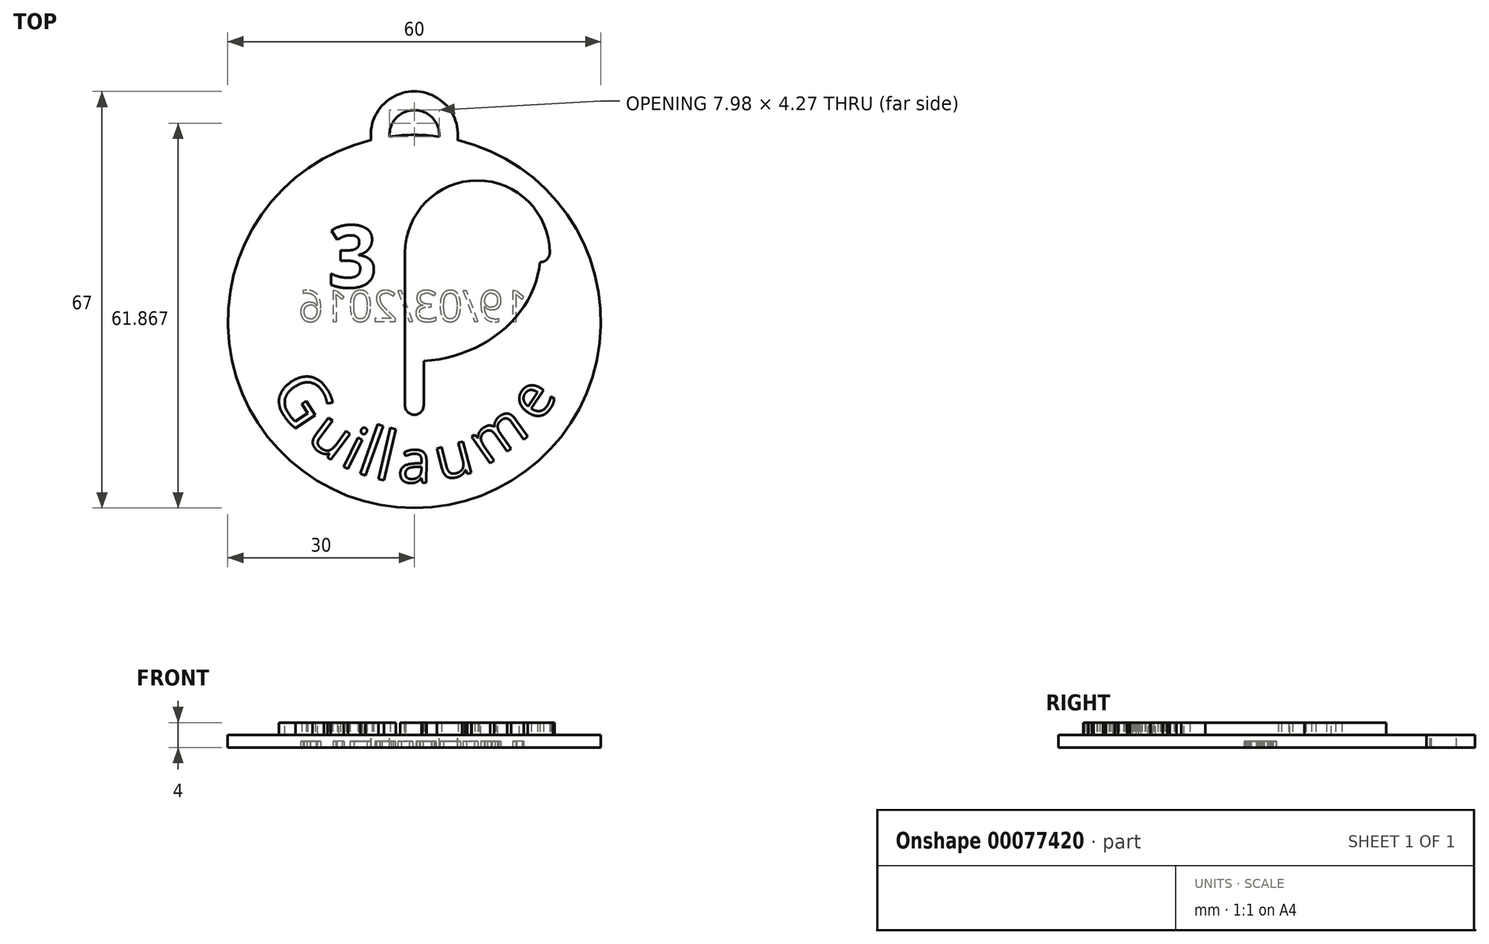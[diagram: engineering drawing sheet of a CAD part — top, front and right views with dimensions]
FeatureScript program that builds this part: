
annotation { "Feature Type Name" : "Feature", "Feature Type Description" : "" }
export const myFeature = defineFeature(function(context is Context, id is Id, definition is map)
    precondition{}
    {
        {
            var Q0;
            Q0=qCreatedBy(makeId("Top.planeOp"),FACE);
            var sketch = newSketch(context, id + "F0", { "sketchPlane" : qUnion([Q0])});
            skCircle(sketch, "E0", {"center": v(0, 0) * mm, "radius": 30 * mm});
            skSolve(sketch);
        }
        {
            var Q0;
            Q0=qSketchRegion(id+"F0",true);
            extrude(context, id + "F1", {"entities" : qUnion([Q0]), "oppositeDirection" : true, "depth" : 2 * mm});
        }
        {
            var Q0;
            Q0=qCreatedBy(makeId("Top.planeOp"),FACE);
            var sketch = newSketch(context, id + "F2", { "sketchPlane" : qUnion([Q0])});
            skEllipticalArc(sketch, "E1", {});
            skLineSegment(sketch, "E2", {"start": v(0, 0) * mm, "end": v(0, 30) * mm, "construction": true});
            skLineSegment(sketch, "E3", {"start": v(0, 11.04) * mm, "end": v(0, -13.5) * mm});
            skArc(sketch, "E4", {"start": v(20.27, 11.04) * mm, "mid": v(10.13, 21.17) * mm, "end": v(0, 11.04) * mm});
            skLineSegment(sketch, "E5", {"start": v(0, 11.04) * mm, "end": v(-16.84, 20.76) * mm, "construction": true});
            skLineSegment(sketch, "E6", {"start": v(0, 11.04) * mm, "end": v(-20.27, 11.04) * mm, "construction": true});
            skArc(sketch, "E7.0.startCap", {"start": v(-1.5, 11.04) * mm, "mid": v(0, 12.54) * mm, "end": v(1.5, 11.04) * mm});
            skArc(sketch, "E7.0.endCap", {"start": v(1.5, -13.5) * mm, "mid": v(0, -15) * mm, "end": v(-1.5, -13.5) * mm});
            skLineSegment(sketch, "E7.0.left", {"start": v(1.5, 11.04) * mm, "end": v(1.5, -13.5) * mm});
            skLineSegment(sketch, "E7.0.right", {"start": v(-1.5, 11.04) * mm, "end": v(-1.5, -13.5) * mm});
            skArc(sketch, "E8.0.startCap", {"start": v(21.77, 11.04) * mm, "mid": v(20.27, 9.54) * mm, "end": v(18.77, 11.04) * mm});
            skArc(sketch, "E8.0.endCap", {"start": v(1.5, 11.04) * mm, "mid": v(0, 9.54) * mm, "end": v(-1.5, 11.04) * mm});
            skArc(sketch, "E8.0.left", {"start": v(18.77, 11.04) * mm, "mid": v(10.13, 19.67) * mm, "end": v(1.5, 11.04) * mm});
            skArc(sketch, "E8.0.right", {"start": v(21.77, 11.04) * mm, "mid": v(10.13, 22.67) * mm, "end": v(-1.5, 11.04) * mm});
            skArc(sketch, "E8.1.startCap", {"start": v(-18.02, 21.68) * mm, "mid": v(-15.91, 21.95) * mm, "end": v(-15.65, 19.84) * mm});
            skArc(sketch, "E8.1.endCap", {"start": v(18.77, 11.04) * mm, "mid": v(20.27, 12.54) * mm, "end": v(21.77, 11.04) * mm});
            skFitSpline(sketch, "E8.1.left", {"points": [v(18.7, 9.5) * mm, v(18.8, 11.04) * mm, v(18.7, 12.6) * mm, v(18.36, 14.63) * mm, v(17.66, 16.6) * mm, v(16.63, 18.49) * mm, v(15.37, 20.3) * mm, v(13.44, 22.32) * mm, v(11.07, 24) * mm, v(8.94, 25.1) * mm, v(6.7, 26.01) * mm, v(4.32, 26.63) * mm, v(1.87, 26.95) * mm, v(0, 27.03) * mm, v(-1.87, 26.95) * mm, v(-4.32, 26.63) * mm, v(-6.7, 26.01) * mm, v(-8.94, 25.1) * mm, v(-11.07, 24) * mm, v(-13.44, 22.32) * mm, v(-15.37, 20.3) * mm, v(-16.63, 18.49) * mm, v(-17.66, 16.6) * mm, v(-18.36, 14.63) * mm, v(-18.7, 12.6) * mm, v(-18.8, 11.04) * mm, v(-18.7, 9.5) * mm, v(-18.36, 7.46) * mm, v(-17.66, 5.48) * mm, v(-16.63, 3.6) * mm, v(-15.37, 1.8) * mm, v(-13.44, -0.24) * mm, v(-11.07, -1.92) * mm, v(-8.94, -3.02) * mm, v(-6.7, -3.93) * mm, v(-4.32, -4.55) * mm, v(-1.87, -4.86) * mm, v(0, -4.94) * mm, v(1.87, -4.86) * mm, v(4.32, -4.55) * mm, v(6.7, -3.93) * mm, v(8.94, -3.02) * mm, v(11.07, -1.92) * mm, v(13.44, -0.24) * mm, v(15.37, 1.8) * mm, v(16.63, 3.6) * mm, v(17.66, 5.48) * mm, v(18.36, 7.46) * mm, v(18.7, 9.5) * mm, v(18.8, 11.04) * mm, v(18.7, 12.6) * mm]});
            skFitSpline(sketch, "E8.1.right", {"points": [v(21.7, 9.15) * mm, v(21.8, 11.04) * mm, v(21.7, 12.93) * mm, v(21.27, 15.42) * mm, v(20.42, 17.81) * mm, v(19.18, 20.07) * mm, v(17.69, 22.22) * mm, v(15.4, 24.61) * mm, v(12.65, 26.56) * mm, v(10.2, 27.83) * mm, v(7.62, 28.88) * mm, v(4.92, 29.58) * mm, v(2.12, 29.94) * mm, v(0, 30.03) * mm, v(-2.12, 29.94) * mm, v(-4.92, 29.58) * mm, v(-7.62, 28.88) * mm, v(-10.2, 27.83) * mm, v(-12.65, 26.56) * mm, v(-15.4, 24.61) * mm, v(-17.69, 22.22) * mm, v(-19.18, 20.07) * mm, v(-20.42, 17.81) * mm, v(-21.27, 15.42) * mm, v(-21.7, 12.93) * mm, v(-21.8, 11.04) * mm, v(-21.7, 9.15) * mm, v(-21.27, 6.67) * mm, v(-20.42, 4.27) * mm, v(-19.18, 2) * mm, v(-17.69, -0.14) * mm, v(-15.4, -2.53) * mm, v(-12.65, -4.48) * mm, v(-10.2, -5.75) * mm, v(-7.62, -6.8) * mm, v(-4.92, -7.5) * mm, v(-2.12, -7.86) * mm, v(0, -7.95) * mm, v(2.12, -7.86) * mm, v(4.92, -7.5) * mm, v(7.62, -6.8) * mm, v(10.2, -5.75) * mm, v(12.65, -4.48) * mm, v(15.4, -2.53) * mm, v(17.69, -0.14) * mm, v(19.18, 2) * mm, v(20.42, 4.27) * mm, v(21.27, 6.67) * mm, v(21.7, 9.15) * mm, v(21.8, 11.04) * mm, v(21.7, 12.93) * mm]});
            const initialGuessF2  = {"E1": [0, 0.011041626236194823, 1, 0, 0.020266667008310185, 0.017458373763805178, 2.5511335140588507, 0]};
            skSetInitialGuess(sketch, initialGuessF2);
            skSolve(sketch);
        }
        {
            var Q0;
            {var subQ0=sQuery(id+"F2.wireOp",EDGE,"E8.1.startCap");Q0=makeQuery(id+"F2.imprint","IMPRINT",FACE,{"disambiguationData":[TD([[makeQuery(id+"F2.imprint","IMPRINT",EDGE,{"derivedFrom":subQ0}),-1.0]])]});}
            var Q1;
            {var subQ0=sQuery(id+"F2.wireOp",EDGE,"E7.0.right");var subQ1=sQuery(id+"F2.wireOp",EDGE,"E1");var subQ2=makeQuery(id+"F2.imprint","INTERSECT",VERTEX,{"derivedFrom":[subQ1,subQ0]});Q1=makeQuery(id+"F2.imprint","IMPRINT",FACE,{"disambiguationData":[TD([[makeQuery(id+"F2.imprint","IMPRINT",EDGE,{"disambiguationData":[TD([[subQ2,-1.0]])],"derivedFrom":subQ1}),1.0]])]});}
            var Q2;
            {var subQ0=sQuery(id+"F2.wireOp",EDGE,"E3");var subQ1=sQuery(id+"F2.wireOp",EDGE,"E1");var subQ2=makeQuery(id+"F2.imprint","INTERSECT",VERTEX,{"derivedFrom":[subQ1,subQ0]});Q2=makeQuery(id+"F2.imprint","IMPRINT",FACE,{"disambiguationData":[TD([[makeQuery(id+"F2.imprint","IMPRINT",EDGE,{"disambiguationData":[TD([[subQ2,-1.0]])],"derivedFrom":subQ1}),1.0]])]});}
            var Q3;
            {var subQ0=sQuery(id+"F2.wireOp",EDGE,"E7.0.right");var subQ1=sQuery(id+"F2.wireOp",EDGE,"E1");var subQ2=makeQuery(id+"F2.imprint","INTERSECT",VERTEX,{"derivedFrom":[subQ1,subQ0]});Q3=makeQuery(id+"F2.imprint","IMPRINT",FACE,{"disambiguationData":[TD([[makeQuery(id+"F2.imprint","IMPRINT",EDGE,{"disambiguationData":[TD([[subQ2,-1.0]])],"derivedFrom":subQ1}),-1.0]])]});}
            var Q4;
            {var subQ0=sQuery(id+"F2.wireOp",EDGE,"E3");var subQ1=sQuery(id+"F2.wireOp",EDGE,"E1");var subQ2=makeQuery(id+"F2.imprint","INTERSECT",VERTEX,{"derivedFrom":[subQ1,subQ0]});Q4=makeQuery(id+"F2.imprint","IMPRINT",FACE,{"disambiguationData":[TD([[makeQuery(id+"F2.imprint","IMPRINT",EDGE,{"disambiguationData":[TD([[subQ2,-1.0]])],"derivedFrom":subQ1}),-1.0]])]});}
            var Q5;
            {var subQ0=sQuery(id+"F2.wireOp",EDGE,"E7.0.left");var subQ1=sQuery(id+"F2.wireOp",EDGE,"E1");var subQ2=makeQuery(id+"F2.imprint","INTERSECT",VERTEX,{"derivedFrom":[subQ1,subQ0]});Q5=makeQuery(id+"F2.imprint","IMPRINT",FACE,{"disambiguationData":[TD([[makeQuery(id+"F2.imprint","IMPRINT",EDGE,{"disambiguationData":[TD([[subQ2,-1.0]])],"derivedFrom":subQ1}),-1.0]])]});}
            var Q6;
            {var subQ0=sQuery(id+"F2.wireOp",EDGE,"E7.0.left");var subQ1=sQuery(id+"F2.wireOp",EDGE,"E1");var subQ2=makeQuery(id+"F2.imprint","INTERSECT",VERTEX,{"derivedFrom":[subQ1,subQ0]});Q6=makeQuery(id+"F2.imprint","IMPRINT",FACE,{"disambiguationData":[TD([[makeQuery(id+"F2.imprint","IMPRINT",EDGE,{"disambiguationData":[TD([[subQ2,-1.0]])],"derivedFrom":subQ1}),1.0]])]});}
            var Q7;
            {var subQ0=sQuery(id+"F2.wireOp",EDGE,"E4");var subQ1=sQuery(id+"F2.wireOp",EDGE,"E1");var subQ2=makeQuery(id+"F2.imprint","INTERSECT",VERTEX,{"derivedFrom":[subQ1,subQ0]});Q7=makeQuery(id+"F2.imprint","IMPRINT",FACE,{"disambiguationData":[TD([[makeQuery(id+"F2.imprint","IMPRINT",EDGE,{"disambiguationData":[TD([[subQ2,1.0]])],"derivedFrom":subQ1}),-1.0]])]});}
            var Q8;
            {var subQ0=sQuery(id+"F2.wireOp",EDGE,"E4");var subQ1=sQuery(id+"F2.wireOp",EDGE,"E1");var subQ2=makeQuery(id+"F2.imprint","INTERSECT",VERTEX,{"derivedFrom":[subQ1,subQ0]});Q8=makeQuery(id+"F2.imprint","IMPRINT",FACE,{"disambiguationData":[TD([[makeQuery(id+"F2.imprint","IMPRINT",EDGE,{"disambiguationData":[TD([[subQ2,1.0]])],"derivedFrom":subQ1}),1.0]])]});}
            var Q9;
            {var subQ5=sQuery(id+"F2.wireOp",EDGE,"E8.0.left");Q9=makeQuery(id+"F2.imprint","IMPRINT",FACE,{"disambiguationData":[TD([[makeQuery(id+"F2.imprint","IMPRINT",EDGE,{"derivedFrom":subQ5}),-1.0]])]});}
            var Q10;
            {var subQ5=sQuery(id+"F2.wireOp",EDGE,"E8.0.right");Q10=makeQuery(id+"F2.imprint","IMPRINT",FACE,{"disambiguationData":[TD([[makeQuery(id+"F2.imprint","IMPRINT",EDGE,{"derivedFrom":subQ5}),1.0]])]});}
            var Q11;
            {var subQ0=sQuery(id+"F2.wireOp",EDGE,"E4");var subQ1=sQuery(id+"F2.wireOp",EDGE,"E3");var subQ2=makeQuery(id+"F2.imprint","INTERSECT",VERTEX,{"derivedFrom":[subQ1,subQ0]});Q11=makeQuery(id+"F2.imprint","IMPRINT",FACE,{"disambiguationData":[TD([[makeQuery(id+"F2.imprint","IMPRINT",EDGE,{"disambiguationData":[TD([[subQ2,-1.0]])],"derivedFrom":subQ1}),-1.0]])]});}
            var Q12;
            {var subQ0=sQuery(id+"F2.wireOp",EDGE,"E4");var subQ1=sQuery(id+"F2.wireOp",EDGE,"E3");var subQ2=makeQuery(id+"F2.imprint","INTERSECT",VERTEX,{"derivedFrom":[subQ1,subQ0]});Q12=makeQuery(id+"F2.imprint","IMPRINT",FACE,{"disambiguationData":[TD([[makeQuery(id+"F2.imprint","IMPRINT",EDGE,{"disambiguationData":[TD([[subQ2,-1.0]])],"derivedFrom":subQ1}),1.0]])]});}
            var Q13;
            {var subQ0=sQuery(id+"F2.wireOp",EDGE,"E8.0.endCap");var subQ1=sQuery(id+"F2.wireOp",EDGE,"E3");var subQ2=makeQuery(id+"F2.imprint","INTERSECT",VERTEX,{"derivedFrom":[subQ1,subQ0]});Q13=makeQuery(id+"F2.imprint","IMPRINT",FACE,{"disambiguationData":[TD([[makeQuery(id+"F2.imprint","IMPRINT",EDGE,{"disambiguationData":[TD([[subQ2,-1.0]])],"derivedFrom":subQ1}),-1.0]])]});}
            var Q14;
            {var subQ0=sQuery(id+"F2.wireOp",EDGE,"E8.0.endCap");var subQ1=sQuery(id+"F2.wireOp",EDGE,"E3");var subQ2=makeQuery(id+"F2.imprint","INTERSECT",VERTEX,{"derivedFrom":[subQ1,subQ0]});Q14=makeQuery(id+"F2.imprint","IMPRINT",FACE,{"disambiguationData":[TD([[makeQuery(id+"F2.imprint","IMPRINT",EDGE,{"disambiguationData":[TD([[subQ2,-1.0]])],"derivedFrom":subQ1}),1.0]])]});}
            var Q15;
            {var subQ1=sQuery(id+"F2.wireOp",EDGE,"E7.0.endCap");Q15=makeQuery(id+"F2.imprint","IMPRINT",FACE,{"disambiguationData":[TD([[makeQuery(id+"F2.imprint","IMPRINT",EDGE,{"derivedFrom":subQ1}),-1.0]])]});}
            extrude(context, id + "F3", {"entities" : qUnion([Q0, Q1, Q2, Q3, Q4, Q5, Q6, Q7, Q8, Q9, Q10, Q11, Q12, Q13, Q14, Q15]), "operationType" : NewBodyOperationType.ADD, "depth" : 2 * mm});
        }
        {
            var Q0;
            Q0=qCreatedBy(makeId("Top.planeOp"),FACE);
            var sketch = newSketch(context, id + "F4", { "sketchPlane" : qUnion([Q0])});
            skText(sketch, "E9", { "text": "3", "fontName": "OpenSans-Bold.ttf"});
            skText(sketch, "E10", { "text": "D", "fontName": "OpenSans-Bold.ttf"});
            const initialGuessF4  = {"E9": [-0.0139, 0.0055, 1, 0, 0.01], "E10": [0.0055, 0.0055, 1, 0, 0.01]};
            skSetInitialGuess(sketch, initialGuessF4);
            skSolve(sketch);
        }
        {
            var Q0;
            Q0=qSketchRegion(id+"F4",true);
            extrude(context, id + "F5", {"entities" : qUnion([Q0]), "operationType" : NewBodyOperationType.ADD, "depth" : 2 * mm});
        }
        {
            var Q0;
            {var subQ8=sQuery(id+"F0.wireOp",EDGE,"E0");Q0=makeQuery(id+"F3.boolean.opBoolean","SPLIT",FACE,{"disambiguationData":[TD([makeQuery(id+"F1.opExtrude","SWEPT_FACE",FACE,{"disambiguationData":[OSD([subQ8])]})])],"derivedFrom":makeQuery(id+"F1.opExtrude","CAP_FACE",FACE,{"disambiguationData":[OSD([subQ8])],"isStart":true})});}
            var sketch = newSketch(context, id + "F6", { "sketchPlane" : qUnion([Q0])});
            skCircle(sketch, "E11.0", {"center": v(0, 0) * mm, "radius": 26 * mm, "construction": true});
            skText(sketch, "E12", { "text": "G", "fontName": "OpenSans-Regular.ttf"});
            skText(sketch, "E13", { "text": "u", "fontName": "OpenSans-Regular.ttf"});
            skText(sketch, "E14", { "text": "i", "fontName": "OpenSans-Regular.ttf"});
            skText(sketch, "E15", { "text": "l", "fontName": "OpenSans-Regular.ttf"});
            skText(sketch, "E16", { "text": "l", "fontName": "OpenSans-Regular.ttf"});
            skText(sketch, "E17", { "text": "a", "fontName": "OpenSans-Regular.ttf"});
            skText(sketch, "E18", { "text": "u", "fontName": "OpenSans-Regular.ttf"});
            skText(sketch, "E19", { "text": "m", "fontName": "OpenSans-Regular.ttf"});
            skText(sketch, "E20", { "text": "e", "fontName": "OpenSans-Regular.ttf"});
            const initialGuessF6  = {"E12": [-0.02342, -0.0113, 0.55606, -0.83114, 0.008], "E13": [-0.01755, -0.01918, 0.8008, -0.59892, 0.007], "E14": [-0.0121, -0.023, 0.89971, -0.43648, 0.007], "E15": [-0.00962, -0.02416, 0.94166, -0.33656, 0.008], "E16": [-0.00668, -0.02513, 0.97495, -0.2224, 0.008], "E17": [-0.00273, -0.02586, 0.99987, -0.0163, 0.007], "E18": [0.00419, -0.02566, 0.96624, 0.25765, 0.007], "E19": [0.01153, -0.0233, 0.8146, 0.58002, 0.007], "E20": [0.02008, -0.01651, 0.55866, 0.8294, 0.007]};
            skSetInitialGuess(sketch, initialGuessF6);
            skSolve(sketch);
        }
        {
            var Q0;
            Q0=qSketchRegion(id+"F6",true);
            extrude(context, id + "F7", {"entities" : qUnion([Q0]), "operationType" : NewBodyOperationType.ADD, "depth" : 2 * mm});
        }
        {
            var Q0;
            Q0=qCreatedBy(makeId("Top.planeOp"),FACE);
            var sketch = newSketch(context, id + "F8", { "sketchPlane" : qUnion([Q0])});
            skArc(sketch, "E21", {"start": v(5.48, 29.5) * mm, "mid": v(0, 35.5) * mm, "end": v(-5.48, 29.5) * mm});
            skArc(sketch, "E22.0.startCap", {"start": v(6.97, 29.36) * mm, "mid": v(5.34, 28) * mm, "end": v(3.98, 29.63) * mm});
            skArc(sketch, "E22.0.endCap", {"start": v(-3.98, 29.63) * mm, "mid": v(-5.34, 28) * mm, "end": v(-6.97, 29.36) * mm});
            skArc(sketch, "E22.0.left", {"start": v(3.98, 29.63) * mm, "mid": v(0, 34) * mm, "end": v(-3.98, 29.63) * mm});
            skArc(sketch, "E22.0.right", {"start": v(6.97, 29.36) * mm, "mid": v(0, 37) * mm, "end": v(-6.97, 29.36) * mm});
            skSolve(sketch);
        }
        {
            var Q0;
            Q0=qSketchRegion(id+"F8",true);
            extrude(context, id + "F9", {"entities" : qUnion([Q0]), "operationType" : NewBodyOperationType.ADD, "oppositeDirection" : true, "depth" : 2 * mm});
        }
        {
            var Q0;
            Q0=makeQuery(id+"F9.boolean.opBoolean","MERGE",FACE,{"derivedFrom":[makeQuery(id+"F1.opExtrude","CAP_FACE",FACE,{"disambiguationData":[OSD([sQuery(id+"F0.wireOp",EDGE,"E0")])],"isStart":false}),makeQuery(id+"F9.opExtrude","CAP_FACE",FACE,{"disambiguationData":[OSD([sQuery(id+"F8.wireOp",EDGE,"E22.0.startCap"),sQuery(id+"F8.wireOp",EDGE,"E22.0.endCap"),sQuery(id+"F8.wireOp",EDGE,"E22.0.left"),sQuery(id+"F8.wireOp",EDGE,"E22.0.right")])],"isStart":false})]});
            var sketch = newSketch(context, id + "F10", { "sketchPlane" : qUnion([Q0])});
            skText(sketch, "E23", { "text": "19/03/2016", "fontName": "OpenSans-Regular.ttf"});
            const initialGuessF10  = {"E23": [0.01826, 0, -1, 0, 0.005]};
            skSetInitialGuess(sketch, initialGuessF10);
            skSolve(sketch);
        }
        {
            var Q0;
            Q0=qSketchRegion(id+"F10",true);
            extrude(context, id + "F11", {"entities" : qUnion([Q0]), "operationType" : NewBodyOperationType.REMOVE, "oppositeDirection" : true, "depth" : 1 * mm});
        }
    });
